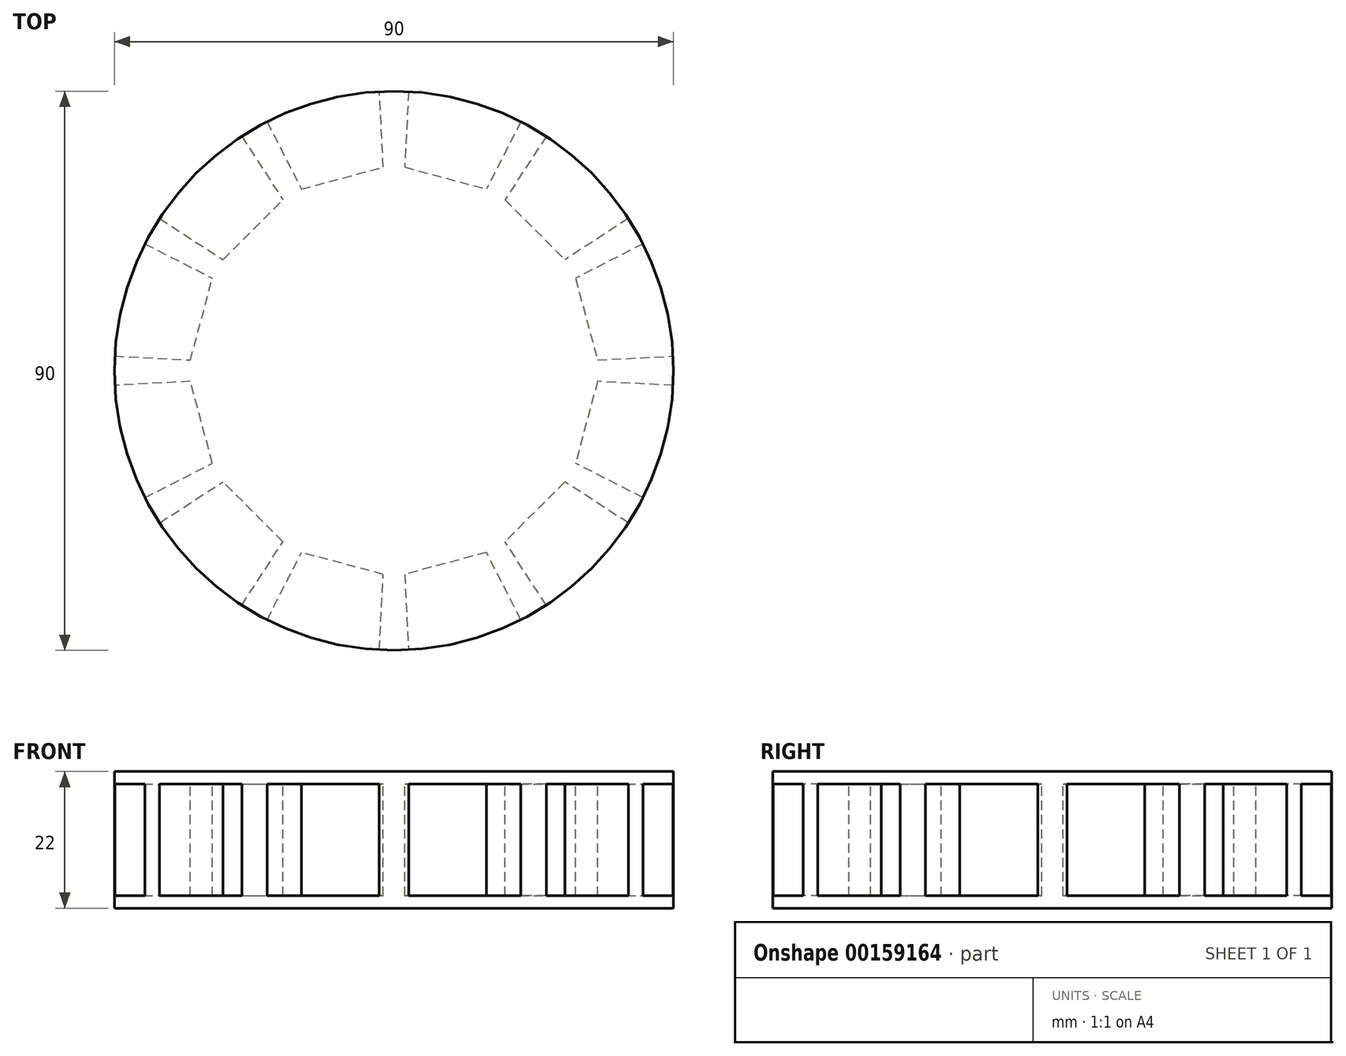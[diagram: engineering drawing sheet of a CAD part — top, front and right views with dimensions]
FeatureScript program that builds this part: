
annotation { "Feature Type Name" : "Feature", "Feature Type Description" : "" }
export const myFeature = defineFeature(function(context is Context, id is Id, definition is map)
    precondition{}
    {
        {
            var Q0;
            Q0=qCreatedBy(makeId("Top.planeOp"),FACE);
            var sketch = newSketch(context, id + "F0", { "sketchPlane" : qUnion([Q0])});
            skCircle(sketch, "E0", {"center": v(0, 0) * mm, "radius": 45 * mm});
            skSolve(sketch);
        }
        {
            var Q0;
            Q0 = qSketchRegion(id + "F0", true);
            extrude(context, id + "F1", {"entities" : qUnion([Q0]), "depth" : 20 * mm});
        }
        {
            var Q0;
            Q0=makeQuery(id+"F1.opExtrude","CAP_FACE",FACE,{"disambiguationData":[OSD([sQuery(id+"F0.wireOp",EDGE,"E0")])],"isStart":false});
            var sketch = newSketch(context, id + "F2", { "sketchPlane" : qUnion([Q0])});
            skLineSegment(sketch, "E1", {"start": v(32.77, 1.72) * mm, "end": v(44.94, 2.36) * mm});
            skLineSegment(sketch, "E2", {"start": v(40.1, 20.43) * mm, "end": v(29.24, 14.9) * mm});
            skLineSegment(sketch, "E3", {"start": v(37.74, 24.5) * mm, "end": v(27.52, 17.87) * mm});
            skLineSegment(sketch, "E4", {"start": v(24.5, 37.74) * mm, "end": v(17.87, 27.52) * mm});
            skLineSegment(sketch, "E5", {"start": v(2.36, 44.94) * mm, "end": v(1.72, 32.77) * mm});
            skArc(sketch, "E6", {"start": v(44.94, 2.36) * mm, "mid": v(43.47, 11.65) * mm, "end": v(40.1, 20.43) * mm});
            skArc(sketch, "E7.trimOffspring", {"start": v(20.43, 40.1) * mm, "mid": v(11.65, 43.47) * mm, "end": v(2.36, 44.94) * mm});
            skLineSegment(sketch, "E8", {"start": v(20.43, 40.1) * mm, "end": v(14.9, 29.24) * mm});
            skLineSegment(sketch, "E9", {"start": v(1.72, 32.77) * mm, "end": v(14.9, 29.24) * mm});
            skLineSegment(sketch, "E10", {"start": v(17.87, 27.52) * mm, "end": v(27.52, 17.87) * mm});
            skLineSegment(sketch, "E11", {"start": v(29.24, 14.9) * mm, "end": v(32.77, 1.72) * mm});
            skArc(sketch, "E12.trimOffspring", {"start": v(37.74, 24.5) * mm, "mid": v(31.82, 31.82) * mm, "end": v(24.5, 37.74) * mm});
            skLineSegment(sketch, "E13.1.0", {"start": v(-44.94, 2.36) * mm, "end": v(-32.77, 1.72) * mm});
            skArc(sketch, "E13.1.1", {"start": v(-40.1, 20.43) * mm, "mid": v(-43.47, 11.65) * mm, "end": v(-44.94, 2.36) * mm});
            skLineSegment(sketch, "E13.1.2", {"start": v(-40.1, 20.43) * mm, "end": v(-29.24, 14.9) * mm});
            skLineSegment(sketch, "E13.1.3", {"start": v(-32.77, 1.72) * mm, "end": v(-29.24, 14.9) * mm});
            skLineSegment(sketch, "E13.1.4", {"start": v(-37.74, 24.5) * mm, "end": v(-27.52, 17.87) * mm});
            skArc(sketch, "E13.1.5", {"start": v(-24.5, 37.74) * mm, "mid": v(-31.82, 31.82) * mm, "end": v(-37.74, 24.5) * mm});
            skLineSegment(sketch, "E13.1.6", {"start": v(-27.52, 17.87) * mm, "end": v(-17.87, 27.52) * mm});
            skLineSegment(sketch, "E13.1.7", {"start": v(-24.5, 37.74) * mm, "end": v(-17.87, 27.52) * mm});
            skLineSegment(sketch, "E13.1.8", {"start": v(-20.43, 40.1) * mm, "end": v(-14.9, 29.24) * mm});
            skLineSegment(sketch, "E13.1.9", {"start": v(-14.9, 29.24) * mm, "end": v(-1.72, 32.77) * mm});
            skLineSegment(sketch, "E13.1.10", {"start": v(-1.72, 32.77) * mm, "end": v(-2.36, 44.94) * mm});
            skArc(sketch, "E13.1.11", {"start": v(-2.36, 44.94) * mm, "mid": v(-11.65, 43.47) * mm, "end": v(-20.43, 40.1) * mm});
            skLineSegment(sketch, "E13.2.0", {"start": v(-2.36, -44.94) * mm, "end": v(-1.72, -32.77) * mm});
            skArc(sketch, "E13.2.1", {"start": v(-20.43, -40.1) * mm, "mid": v(-11.65, -43.47) * mm, "end": v(-2.36, -44.94) * mm});
            skLineSegment(sketch, "E13.2.2", {"start": v(-20.43, -40.1) * mm, "end": v(-14.9, -29.24) * mm});
            skLineSegment(sketch, "E13.2.3", {"start": v(-1.72, -32.77) * mm, "end": v(-14.9, -29.24) * mm});
            skLineSegment(sketch, "E13.2.4", {"start": v(-24.5, -37.74) * mm, "end": v(-17.87, -27.52) * mm});
            skArc(sketch, "E13.2.5", {"start": v(-37.74, -24.5) * mm, "mid": v(-31.82, -31.82) * mm, "end": v(-24.5, -37.74) * mm});
            skLineSegment(sketch, "E13.2.6", {"start": v(-17.87, -27.52) * mm, "end": v(-27.52, -17.87) * mm});
            skLineSegment(sketch, "E13.2.7", {"start": v(-37.74, -24.5) * mm, "end": v(-27.52, -17.87) * mm});
            skLineSegment(sketch, "E13.2.8", {"start": v(-40.1, -20.43) * mm, "end": v(-29.24, -14.9) * mm});
            skLineSegment(sketch, "E13.2.9", {"start": v(-29.24, -14.9) * mm, "end": v(-32.77, -1.72) * mm});
            skLineSegment(sketch, "E13.2.10", {"start": v(-32.77, -1.72) * mm, "end": v(-44.94, -2.36) * mm});
            skArc(sketch, "E13.2.11", {"start": v(-44.94, -2.36) * mm, "mid": v(-43.47, -11.65) * mm, "end": v(-40.1, -20.43) * mm});
            skLineSegment(sketch, "E13.3.0", {"start": v(44.94, -2.36) * mm, "end": v(32.77, -1.72) * mm});
            skArc(sketch, "E13.3.1", {"start": v(40.1, -20.43) * mm, "mid": v(43.47, -11.65) * mm, "end": v(44.94, -2.36) * mm});
            skLineSegment(sketch, "E13.3.2", {"start": v(40.1, -20.43) * mm, "end": v(29.24, -14.9) * mm});
            skLineSegment(sketch, "E13.3.3", {"start": v(32.77, -1.72) * mm, "end": v(29.24, -14.9) * mm});
            skLineSegment(sketch, "E13.3.4", {"start": v(37.74, -24.5) * mm, "end": v(27.52, -17.87) * mm});
            skArc(sketch, "E13.3.5", {"start": v(24.5, -37.74) * mm, "mid": v(31.82, -31.82) * mm, "end": v(37.74, -24.5) * mm});
            skLineSegment(sketch, "E13.3.6", {"start": v(27.52, -17.87) * mm, "end": v(17.87, -27.52) * mm});
            skLineSegment(sketch, "E13.3.7", {"start": v(24.5, -37.74) * mm, "end": v(17.87, -27.52) * mm});
            skLineSegment(sketch, "E13.3.8", {"start": v(20.43, -40.1) * mm, "end": v(14.9, -29.24) * mm});
            skLineSegment(sketch, "E13.3.9", {"start": v(14.9, -29.24) * mm, "end": v(1.72, -32.77) * mm});
            skLineSegment(sketch, "E13.3.10", {"start": v(1.72, -32.77) * mm, "end": v(2.36, -44.94) * mm});
            skArc(sketch, "E13.3.11", {"start": v(2.36, -44.94) * mm, "mid": v(11.65, -43.47) * mm, "end": v(20.43, -40.1) * mm});
            skSolve(sketch);
        }
        {
            var Q0;
            Q0 = qSketchRegion(id + "F2", true);
            extrude(context, id + "F3", {"entities" : qUnion([Q0]), "operationType" : NewBodyOperationType.REMOVE, "oppositeDirection" : true, "depth" : 18 * mm});
        }
        {
            var Q0;
            Q0=makeQuery(id+"F1.opExtrude","CAP_FACE",FACE,{"disambiguationData":[OSD([sQuery(id+"F0.wireOp",EDGE,"E0")])],"isStart":false});
            var sketch = newSketch(context, id + "F4", { "sketchPlane" : qUnion([Q0])});
            skCircle(sketch, "E14", {"center": v(0, 0) * mm, "radius": 45 * mm});
            skSolve(sketch);
        }
        {
            var Q0;
            Q0 = qSketchRegion(id + "F4", true);
            extrude(context, id + "F5", {"entities" : qUnion([Q0]), "operationType" : NewBodyOperationType.ADD, "depth" : 2 * mm});
        }
    });
